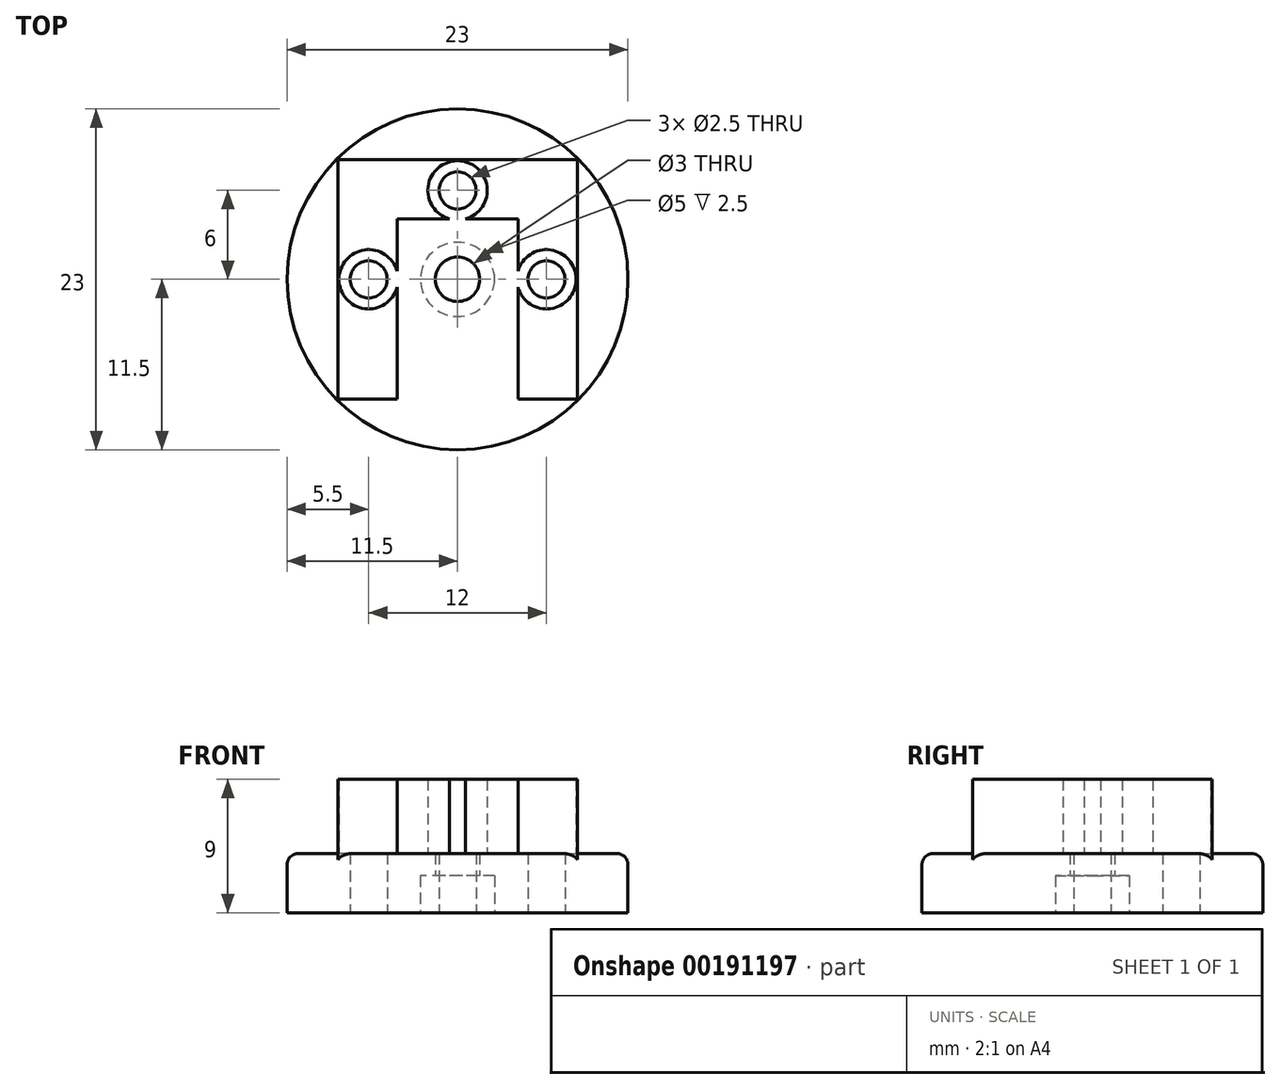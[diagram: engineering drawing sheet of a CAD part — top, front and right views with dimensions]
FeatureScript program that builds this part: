
annotation { "Feature Type Name" : "Feature", "Feature Type Description" : "" }
export const myFeature = defineFeature(function(context is Context, id is Id, definition is map)
    precondition{}
    {
        {
            var Q0;
            Q0=qCreatedBy(makeId("Top.planeOp"),FACE);
            var sketch = newSketch(context, id + "F0", { "sketchPlane" : qUnion([Q0])});
            skCircle(sketch, "E0", {"center": v(0, 0) * mm, "radius": 11.5 * mm});
            skCircle(sketch, "E1", {"center": v(-6, 0) * mm, "radius": 1.25 * mm});
            skCircle(sketch, "E2", {"center": v(6, 0) * mm, "radius": 1.25 * mm});
            skCircle(sketch, "E3", {"center": v(0, 6) * mm, "radius": 1.25 * mm});
            skCircle(sketch, "E4", {"center": v(0, 0) * mm, "radius": 1.5 * mm});
            skSolve(sketch);
        }
        {
            var Q0;
            Q0 = qSketchRegion(id + "F0", true);
            extrude(context, id + "F1", {"entities" : qUnion([Q0]), "depth" : 4 * mm});
        }
        {
            var Q0;
            Q0=makeQuery(id+"F1.opExtrude","CAP_FACE",FACE,{"disambiguationData":[OSD([sQuery(id+"F0.wireOp",EDGE,"E0"),sQuery(id+"F0.wireOp",EDGE,"nGVQfhoY-R6Wu-IyuL-ECj8-tWsw6deZUODL"),sQuery(id+"F0.wireOp",EDGE,"E1"),sQuery(id+"F0.wireOp",EDGE,"E2"),sQuery(id+"F0.wireOp",EDGE,"E3")])],"isStart":false});
            var sketch = newSketch(context, id + "F2", { "sketchPlane" : qUnion([Q0])});
            skLineSegment(sketch, "E5.top", {"start": v(4.08, 4.08) * mm, "end": v(-4.08, 4.07) * mm});
            skLineSegment(sketch, "E5.left", {"start": v(4.08, -4.07) * mm, "end": v(4.08, 4.08) * mm});
            skLineSegment(sketch, "E5.right", {"start": v(-4.08, -4.08) * mm, "end": v(-4.08, 4.07) * mm});
            skPoint(sketch, "E5.middle", {"position": v(0, 0) * mm});
            skLineSegment(sketch, "E6.0", {"start": v(-8.08, -8.08) * mm, "end": v(-8.08, 8.07) * mm});
            skLineSegment(sketch, "E6.1", {"start": v(8.08, -8.07) * mm, "end": v(4.08, -8.07) * mm});
            skLineSegment(sketch, "E6.2", {"start": v(8.08, -8.07) * mm, "end": v(8.08, 8.08) * mm});
            skLineSegment(sketch, "E6.3", {"start": v(8.08, 8.08) * mm, "end": v(-8.08, 8.07) * mm});
            skCircle(sketch, "E7.0", {"center": v(-6, 0) * mm, "radius": 1.25 * mm});
            skCircle(sketch, "E7.1", {"center": v(6, 0) * mm, "radius": 1.25 * mm});
            skCircle(sketch, "E7.3", {"center": v(0, 6) * mm, "radius": 1.25 * mm});
            skCircle(sketch, "E8", {"center": v(-6, 0) * mm, "radius": 2 * mm});
            skCircle(sketch, "E9", {"center": v(6, 0) * mm, "radius": 2 * mm});
            skCircle(sketch, "E10", {"center": v(0, 6) * mm, "radius": 2 * mm});
            skLineSegment(sketch, "E11", {"start": v(-4.08, -4.08) * mm, "end": v(-4.08, -8.07) * mm});
            skLineSegment(sketch, "E12", {"start": v(4.08, -4.07) * mm, "end": v(4.08, -8.07) * mm});
            skLineSegment(sketch, "E13.trimOffspring", {"start": v(-4.07, -8.08) * mm, "end": v(-8.07, -8.08) * mm});
            skSolve(sketch);
        }
        {
            var Q0;
            {var subQ7=sQuery(id+"F2.wireOp",EDGE,"E5.right");var subQ8=sQuery(id+"F2.wireOp",EDGE,"E5.top");var subQ9=makeQuery(id+"F2.imprint","INTERSECT",VERTEX,{"derivedFrom":[subQ8,subQ7]});Q0=makeQuery(id+"F2.imprint","IMPRINT",FACE,{"disambiguationData":[TD([[makeQuery(id+"F2.imprint","IMPRINT",EDGE,{"disambiguationData":[TD([[subQ9,1.0]])],"derivedFrom":subQ8}),-1.0]])]});}
            var Q1;
            {var subQ7=sQuery(id+"F2.wireOp",EDGE,"E5.left");var subQ8=sQuery(id+"F2.wireOp",EDGE,"E5.top");var subQ9=makeQuery(id+"F2.imprint","INTERSECT",VERTEX,{"derivedFrom":[subQ8,subQ7]});Q1=makeQuery(id+"F2.imprint","IMPRINT",FACE,{"disambiguationData":[TD([[makeQuery(id+"F2.imprint","IMPRINT",EDGE,{"disambiguationData":[TD([[subQ9,-1.0]])],"derivedFrom":subQ8}),-1.0]])]});}
            var Q2;
            {var subQ5=sQuery(id+"F2.wireOp",EDGE,"E5.bottom");var subQ8=sQuery(id+"F2.wireOp",EDGE,"E5.left");var subQ11=makeQuery(id+"F2.imprint","INTERSECT",VERTEX,{"derivedFrom":[subQ5,subQ8]});Q2=makeQuery(id+"F2.imprint","IMPRINT",FACE,{"disambiguationData":[TD([[makeQuery(id+"F2.imprint","IMPRINT",EDGE,{"disambiguationData":[TD([[subQ11,-1.0]])],"derivedFrom":subQ5}),1.0]])]});}
            var Q3;
            {var subQ7=sQuery(id+"F2.wireOp",EDGE,"E5.bottom");var subQ9=sQuery(id+"F2.wireOp",EDGE,"E5.right");var subQ10=makeQuery(id+"F2.imprint","INTERSECT",VERTEX,{"derivedFrom":[subQ7,subQ9]});Q3=makeQuery(id+"F2.imprint","IMPRINT",FACE,{"disambiguationData":[TD([[makeQuery(id+"F2.imprint","IMPRINT",EDGE,{"disambiguationData":[TD([[subQ10,1.0]])],"derivedFrom":subQ7}),1.0]])]});}
            extrude(context, id + "F3", {"entities" : qUnion([Q0, Q1, Q2, Q3]), "operationType" : NewBodyOperationType.ADD, "depth" : 5 * mm});
        }
        {
            var Q0;
            Q0=makeQuery(id+"F1.opExtrude","CAP_EDGE",EDGE,{"disambiguationData":[OSD([sQuery(id+"F0.wireOp",EDGE,"E0")])],"isStart":false});
            fillet(context, id + "F4", {"entities" : qUnion([Q0]), "radius" : .75 * mm, "tangentPropagation" : true, "allowEdgeOverflow" : false});
        }
        {
            var Q0;
            Q0=makeQuery(id+"F0.imprint","IMPRINT",FACE,{"disambiguationData":[TD([[makeQuery(id+"F0.imprint","IMPRINT",EDGE,{"derivedFrom":sQuery(id+"F0.wireOp",EDGE,"E0")}),1.0]])]});
            var sketch = newSketch(context, id + "F5", { "sketchPlane" : qUnion([Q0])});
            skCircle(sketch, "E14", {"center": v(0, 0) * mm, "radius": 2.5 * mm});
            skCircle(sketch, "E15.0", {"center": v(0, 0) * mm, "radius": 1.5 * mm});
            skSolve(sketch);
        }
        {
            var Q0;
            Q0=makeQuery(id+"F5.imprint","IMPRINT",FACE,{"disambiguationData":[TD([[makeQuery(id+"F5.imprint","IMPRINT",EDGE,{"derivedFrom":sQuery(id+"F5.wireOp",EDGE,"E14")}),1.0]])]});
            extrude(context, id + "F6", {"entities" : qUnion([Q0]), "operationType" : NewBodyOperationType.REMOVE, "depth" : 2.5 * mm});
        }
    });
